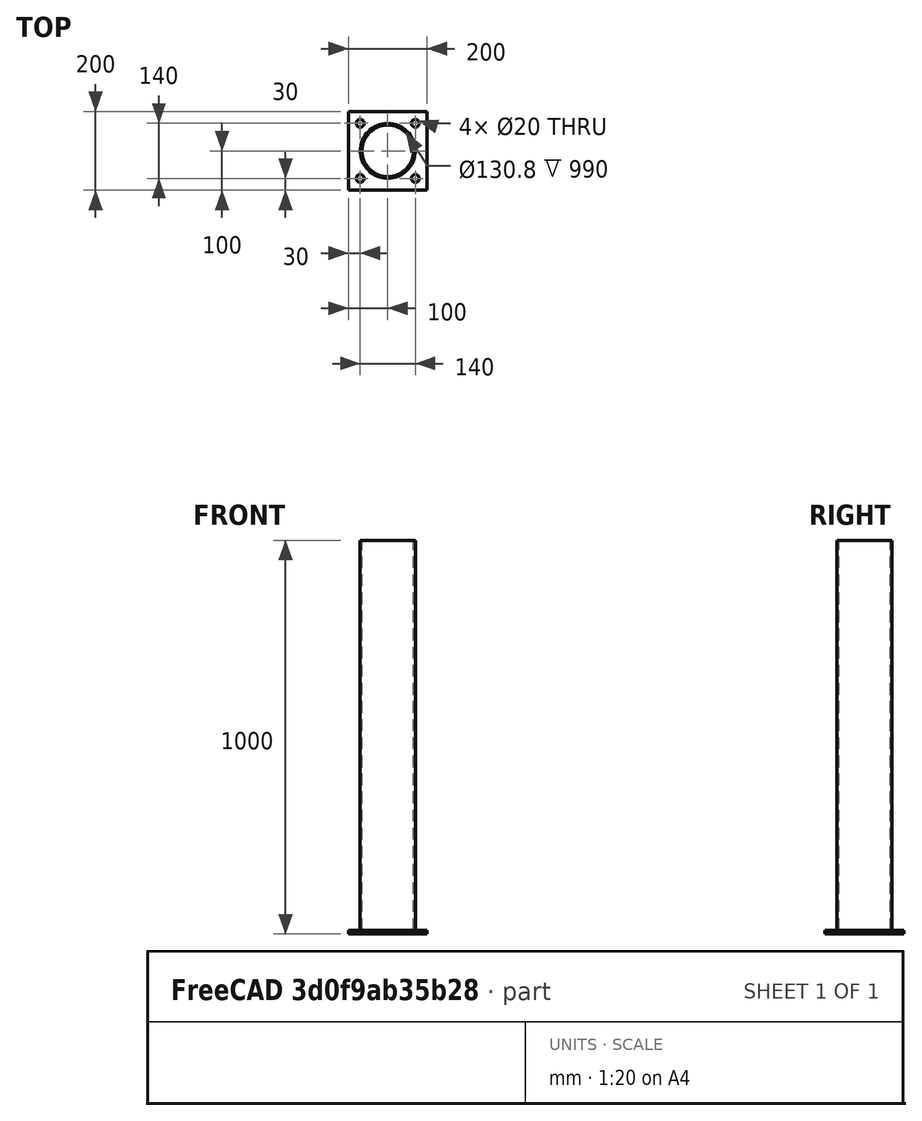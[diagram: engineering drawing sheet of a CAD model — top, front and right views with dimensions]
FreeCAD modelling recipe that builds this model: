
FCSTD DOCUMENT  (FreeCAD 0.21R30492 (Git))
Label: 03_Pst_Pip
License: All rights reserved
LicenseURL: http://en.wikipedia.org/wiki/All_rights_reserved
objects: Part::FeaturePython×2, Part::Extrusion×1, Part::MultiFuse×1
note: 4 computed .brp shape members not serialized (recipe doc carries the construction recipe); baked Part::Feature solids carry a one-line shape summary decoded from their .brp

FEATURE [Part::FeaturePython] BasePlate  # WARN: FeaturePython — macro-defined, semantics opaque (R4)
  B = 200
  D = 20
  H = 200
  b1 = 30
  h1 = 30
  sface = 0
FEATURE [Part::Extrusion] Extrude
  Base = -> BasePlate
  Dir = (0,0,1)
  DirMode = 2
  FaceMakerClass = Part::FaceMakerBullseye
  LengthFwd = 10
  LengthRev = 0
  Solid = true
  Symmetric = false
FEATURE [Part::FeaturePython] Pipe  # WARN: FeaturePython — macro-defined, semantics opaque (R4)
  D = 139.8
  L = 1000
  Solid = true
  g0 = 7.85
  mass = 15.0152
  size = 12
  standard = SGP
  t = 4.5
FEATURE [Part::MultiFuse] Fusion  label="PostPipe"
  Shapes = -> [Extrude,Pipe]
